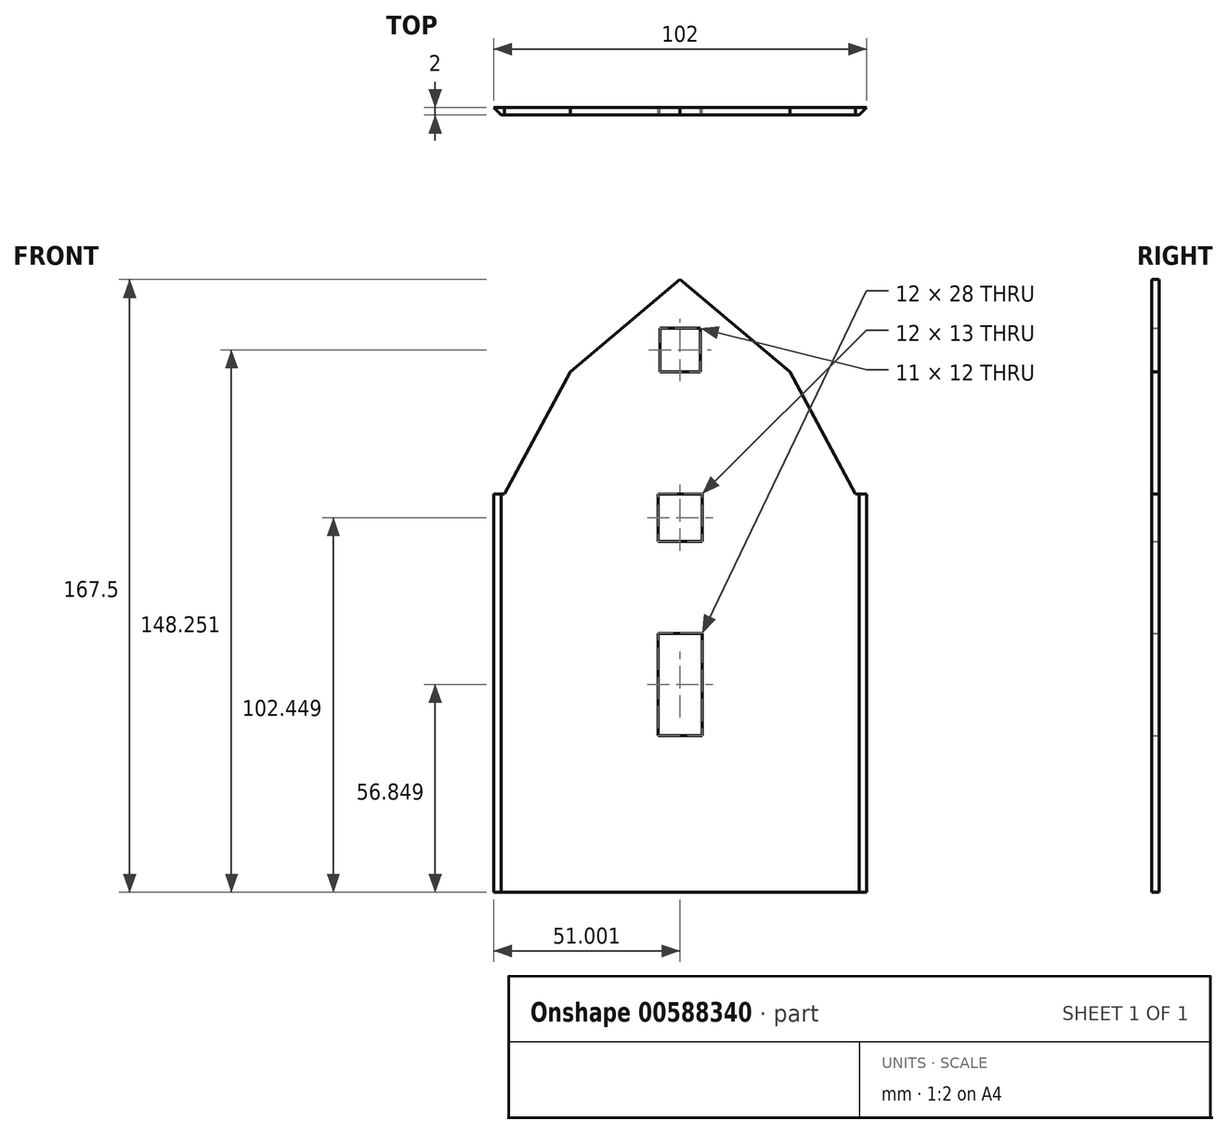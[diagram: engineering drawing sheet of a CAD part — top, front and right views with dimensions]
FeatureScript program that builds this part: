
annotation { "Feature Type Name" : "Feature", "Feature Type Description" : "" }
export const myFeature = defineFeature(function(context is Context, id is Id, definition is map)
    precondition{}
    {
        {
            var Q0;
            Q0=qCreatedBy(makeId("Front.planeOp"),FACE);
            var sketch = newSketch(context, id + "F0", { "sketchPlane" : qUnion([Q0])});
            skLineSegment(sketch, "E0", {"start": v(139.3, 69.08) * mm, "end": v(127.3, 69.08) * mm});
            skLineSegment(sketch, "E1", {"start": v(133.3, -39.87) * mm, "end": v(85.3, -39.87) * mm});
            skLineSegment(sketch, "E2", {"start": v(133.3, 69.08) * mm, "end": v(139.3, 69.08) * mm});
            skLineSegment(sketch, "E3", {"start": v(127.3, 69.08) * mm, "end": v(139.3, 69.08) * mm});
            skPoint(sketch, "E4.trimOffspring.end.orphan", {"position": v(133.3, -39.87) * mm});
            skLineSegment(sketch, "E5", {"start": v(163.3, 102.38) * mm, "end": v(181.3, 69.08) * mm});
            skLineSegment(sketch, "E6", {"start": v(133.3, 127.63) * mm, "end": v(163.3, 102.38) * mm});
            skLineSegment(sketch, "E7", {"start": v(138.8, 102.38) * mm, "end": v(127.8, 102.38) * mm});
            skLineSegment(sketch, "E8", {"start": v(133.3, 127.63) * mm, "end": v(103.3, 102.38) * mm});
            skLineSegment(sketch, "E9", {"start": v(85.3, 69.08) * mm, "end": v(103.3, 102.38) * mm});
            skLineSegment(sketch, "E10", {"start": v(133.3, 102.38) * mm, "end": v(127.8, 102.38) * mm});
            skLineSegment(sketch, "E11", {"start": v(127.8, 102.38) * mm, "end": v(127.8, 114.38) * mm});
            skLineSegment(sketch, "E12", {"start": v(127.8, 114.38) * mm, "end": v(138.8, 114.38) * mm});
            skLineSegment(sketch, "E13", {"start": v(138.8, 114.38) * mm, "end": v(138.8, 102.38) * mm});
            skLineSegment(sketch, "E14", {"start": v(138.8, 102.38) * mm, "end": v(133.3, 102.38) * mm});
            skLineSegment(sketch, "E15", {"start": v(85.3, 69.08) * mm, "end": v(82.3, 69.08) * mm});
            skLineSegment(sketch, "E16", {"start": v(181.3, 69.08) * mm, "end": v(184.3, 69.08) * mm});
            skLineSegment(sketch, "E17", {"start": v(184.3, -39.87) * mm, "end": v(184.3, 69.08) * mm});
            skLineSegment(sketch, "E18", {"start": v(85.3, -39.87) * mm, "end": v(82.3, -39.87) * mm});
            skLineSegment(sketch, "E19", {"start": v(82.3, -39.87) * mm, "end": v(82.3, 69.08) * mm});
            skLineSegment(sketch, "E20", {"start": v(133.3, -39.87) * mm, "end": v(184.3, -39.87) * mm});
            skLineSegment(sketch, "E21", {"start": v(127.3, 30.98) * mm, "end": v(139.3, 30.98) * mm});
            skLineSegment(sketch, "E22", {"start": v(139.3, 30.98) * mm, "end": v(139.3, 0) * mm});
            skLineSegment(sketch, "E23", {"start": v(127.3, 0) * mm, "end": v(127.3, 30.98) * mm});
            skLineSegment(sketch, "E24", {"start": v(127.3, 30.98) * mm, "end": v(127.3, 2.98) * mm});
            skLineSegment(sketch, "E25", {"start": v(127.3, 2.98) * mm, "end": v(139.3, 2.98) * mm});
            skLineSegment(sketch, "E26", {"start": v(127.3, 69.08) * mm, "end": v(127.3, 56.08) * mm});
            skLineSegment(sketch, "E27", {"start": v(127.3, 56.08) * mm, "end": v(139.3, 56.08) * mm});
            skLineSegment(sketch, "E28", {"start": v(139.3, 69.08) * mm, "end": v(139.3, 56.08) * mm});
            skLineSegment(sketch, "E29", {"start": v(184.3, -39.87) * mm, "end": v(184.3, -11.24) * mm});
            skSolve(sketch);
        }
        {
            var Q0;
            Q0=makeQuery(id+"F0.imprint","IMPRINT",FACE,{"disambiguationData":[TD([[makeQuery(id+"F0.imprint","IMPRINT",EDGE,{"derivedFrom":sQuery(id+"F0.wireOp",EDGE,"E1")}),-1.0]])]});
            extrude(context, id + "F1", {"entities" : qUnion([Q0]), "depth" : 2 * mm, "offsetDistance" : 25 * mm});
        }
        {
            var Q0;
            Q0=makeQuery(id+"F1.opExtrude","SWEPT_FACE",FACE,{"disambiguationData":[OSD([sQuery(id+"F0.wireOp",EDGE,"E16")])]});
            var sketch = newSketch(context, id + "F2", { "sketchPlane" : qUnion([Q0])});
            skLineSegment(sketch, "E30", {"start": v(184.3, -2) * mm, "end": v(182.3, -2) * mm});
            skLineSegment(sketch, "E31", {"start": v(184.3, 0) * mm, "end": v(184.3, -2) * mm});
            skLineSegment(sketch, "E32", {"start": v(182.3, -2) * mm, "end": v(184.3, 0) * mm});
            skSolve(sketch);
        }
        {
            var Q0;
            Q0=makeQuery(id+"F2.imprint","IMPRINT",FACE,{"disambiguationData":[TD([[makeQuery(id+"F2.imprint","IMPRINT",EDGE,{"derivedFrom":sQuery(id+"F2.wireOp",EDGE,"E30")}),1.0]])]});
            extrude(context, id + "F3", {"entities" : qUnion([Q0]), "operationType" : NewBodyOperationType.REMOVE, "oppositeDirection" : true, "depth" : 250 * mm, "offsetDistance" : 25 * mm});
        }
        {
            var Q0;
            Q0=makeQuery(id+"F1.opExtrude","SWEPT_FACE",FACE,{"disambiguationData":[OSD([sQuery(id+"F0.wireOp",EDGE,"E15")])]});
            var sketch = newSketch(context, id + "F4", { "sketchPlane" : qUnion([Q0])});
            skLineSegment(sketch, "E33", {"start": v(82.3, -2) * mm, "end": v(84.3, -2) * mm});
            skLineSegment(sketch, "E34", {"start": v(82.3, 0) * mm, "end": v(84.3, -2) * mm});
            skLineSegment(sketch, "E35", {"start": v(84.3, -2) * mm, "end": v(82.3, -2) * mm});
            skSolve(sketch);
        }
        {
            var Q0;
            Q0=makeQuery(id+"F4.imprint","IMPRINT",FACE,{"disambiguationData":[TD([[makeQuery(id+"F4.imprint","IMPRINT",EDGE,{"derivedFrom":sQuery(id+"F4.wireOp",EDGE,"E34")}),-1.0]])]});
            extrude(context, id + "F5", {"entities" : qUnion([Q0]), "operationType" : NewBodyOperationType.REMOVE, "oppositeDirection" : true, "depth" : 250 * mm, "offsetDistance" : 25 * mm});
        }
    });
